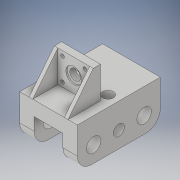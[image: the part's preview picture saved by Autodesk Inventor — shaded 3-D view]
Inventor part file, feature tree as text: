
AUTODESK INVENTOR PART (.ipt)
format: ipt  version: 2019 (Build 230136000, 136)  size: 232,960 bytes
history: native  units: mm
features: sketch x8, extrude x7, hole x4, fillet x1
ambient origin geometry x8: Origin, YZ Plane, XZ Plane, XY Plane, X Axis, Y Axis, Z Axis, Center Point
bodies: Solid1 (feature_tree)
feature tree (20):
  extrude  "Extrusion1"  Depth=80.0mm
  extrude  "Extrusion11"  Depth=20.0mm
  sketch  "Sketch13"  dims[d57=115.0mm d58=37.5mm d59=0.0mm]
  hole  "Hole2"  [1 undecoded]
  hole  "Hole3"  [1 undecoded]
  hole  "Hole6"  [1 undecoded]
  fillet  "Fillet19"  Radius=10.0mm
  extrude  "Extrusion15"  Depth=10.0mm TaperAngle=0.0deg
  sketch  "Sketch21"  dims[d112=25.0mm]
  extrude  "Extrusion16"  Depth=15.0mm
  hole  "Hole7"  [1 undecoded]
  extrude  "Extrusion17"  Depth=35.0mm
  extrude  "Extrusion18"  Depth=15.0mm
  extrude  "Extrusion19"  Depth=10.0mm
  sketch  "Sketch1"  dims[d0=115.0mm d1=80.0mm]
  sketch  "Sketch12"  dims[d2=20.0mm d3=0.0mm d56=20.0mm]
  sketch  "Sketch19"  dims[d63=20.0mm d64=6.0mm d65=4.0mm d66=2.0mm d67=90.0deg d68=8.0mm d69=20.594885mm]
  sketch  "Sketch20"  dims[d70=15.0mm d71=6.0mm d72=4.0mm d73=2.0mm d74=90.0deg d75=8.0mm d76=20.594885mm d111=25.0mm]
  sketch  "Sketch24"  dims[d113=15.0mm d114=6.0mm d115=4.0mm d116=2.0mm d117=90.0deg d118=15.0mm d119=0.0mm d120=20.0mm d122=10.0mm]
  sketch  "Sketch25"  dims[d123=44.0mm d124=0.0mm d126=50.0mm d127=0.0mm d128=15.0mm d129=35.0mm d130=35.0mm d131=15.0mm d132=22.0mm d134=15.5mm d135=15.5mm d136=40.0mm d138=360.0deg d140=5.0mm d141=6.0mm d142=4.0mm d143=2.0mm d144=90.0deg d145=15.0mm d146=0.0mm d147=22.0mm d148=2.0mm d149=0.0mm d151=45.0mm d152=54.0mm d155=5.0mm d156=5.0mm d157=44.0mm d158=0.0mm d159=100.0mm d160=0.0mm d161=10.0mm d12=1.0mm d13=1.0mm d14=1.0mm d15=0.15mm d16=0.25mm d17=0.375mm d18=14.3117mm d19=0.75mm d20=20.594885mm d21=0.0625mm d22=0.75mm d23=0.375mm]
note: 4 required parameter values undecoded (feature->parameter linkage not recoverable at this tier; creation-order binding heuristic only, values carry confidence <= 0.55)
